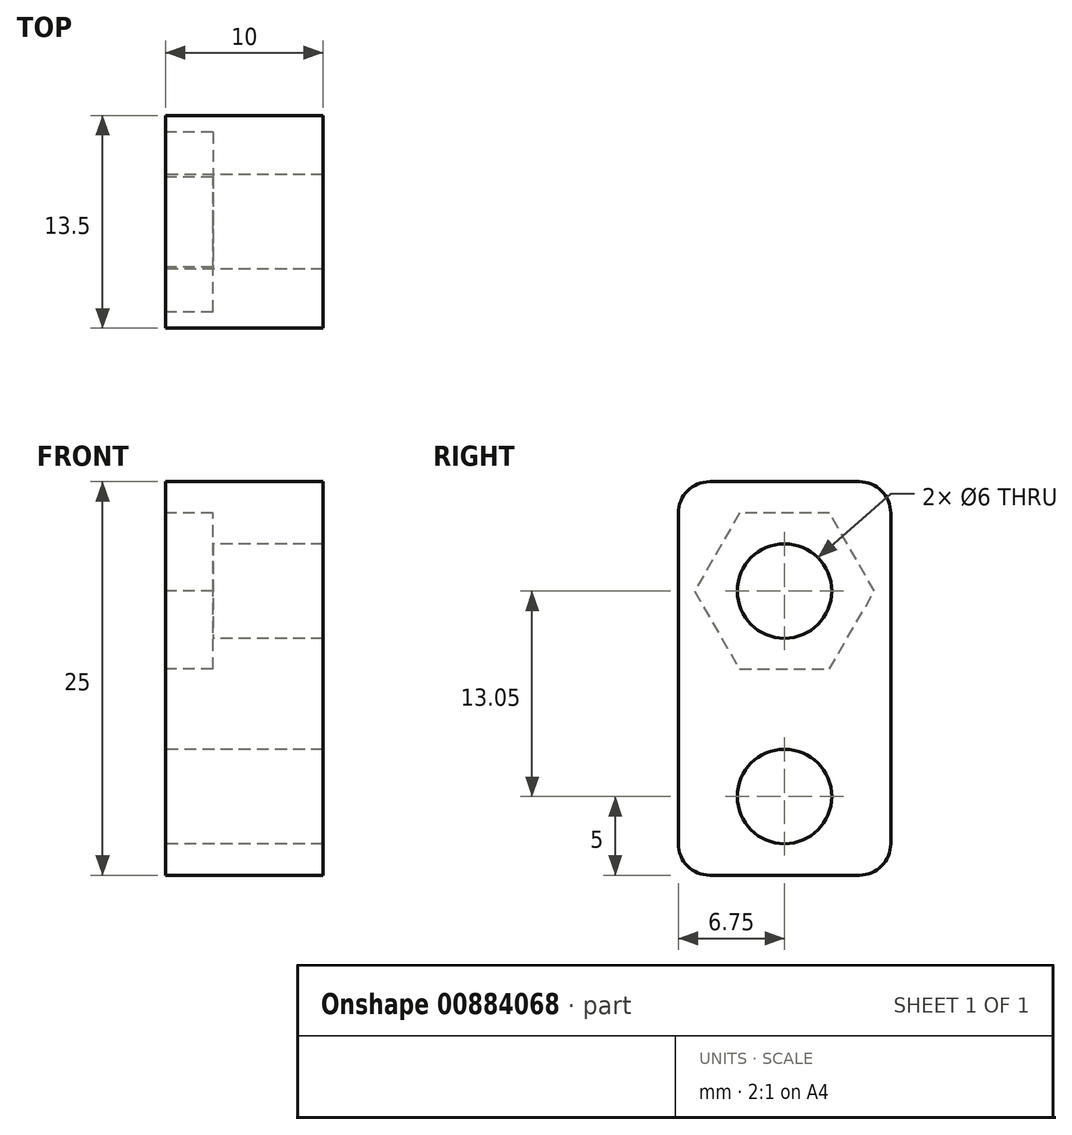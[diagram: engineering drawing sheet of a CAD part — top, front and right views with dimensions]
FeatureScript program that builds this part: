
annotation { "Feature Type Name" : "Feature", "Feature Type Description" : "" }
export const myFeature = defineFeature(function(context is Context, id is Id, definition is map)
    precondition{}
    {
        {
            var Q0;
            Q0=qCreatedBy(makeId("Top.planeOp"),FACE);
            var sketch = newSketch(context, id + "F0", { "sketchPlane" : qUnion([Q0])});
            skLineSegment(sketch, "E0.bottom", {"start": v(5, 6.75) * mm, "end": v(-5, 6.75) * mm});
            skLineSegment(sketch, "E0.top", {"start": v(5, -6.75) * mm, "end": v(-5, -6.75) * mm});
            skLineSegment(sketch, "E0.left", {"start": v(5, 6.75) * mm, "end": v(5, -6.75) * mm});
            skLineSegment(sketch, "E0.right", {"start": v(-5, 6.75) * mm, "end": v(-5, -6.75) * mm});
            skPoint(sketch, "E0.middle", {"position": v(0, 0) * mm});
            skSolve(sketch);
        }
        {
            var Q0;
            Q0 = qSketchRegion(id + "F0", true);
            extrude(context, id + "F1", {"entities" : qUnion([Q0]), "depth" : 25 * mm, "offsetDistance" : 25 * mm});
        }
        {
            var Q0;
            Q0=makeQuery(id+"F1.opExtrude","SWEPT_FACE",FACE,{"disambiguationData":[OSD([sQuery(id+"F0.wireOp",EDGE,"E0.right")])]});
            var sketch = newSketch(context, id + "F2", { "sketchPlane" : qUnion([Q0])});
            skCircle(sketch, "E1.cCircle", {"center": v(0, 18.05) * mm, "radius": 4.95 * mm, "construction": true});
            skLineSegment(sketch, "E1.0", {"start": v(-2.86, 23) * mm, "end": v(2.86, 23) * mm});
            skLineSegment(sketch, "E1.1", {"start": v(2.86, 23) * mm, "end": v(5.72, 18.05) * mm});
            skLineSegment(sketch, "E1.2", {"start": v(5.72, 18.05) * mm, "end": v(2.86, 13.1) * mm});
            skLineSegment(sketch, "E1.3", {"start": v(2.86, 13.1) * mm, "end": v(-2.86, 13.1) * mm});
            skLineSegment(sketch, "E1.4", {"start": v(-2.86, 13.1) * mm, "end": v(-5.72, 18.05) * mm});
            skLineSegment(sketch, "E1.5", {"start": v(-5.72, 18.05) * mm, "end": v(-2.86, 23) * mm});
            skPoint(sketch, "E1.0.midPoint", {"position": v(0, 23) * mm});
            skCircle(sketch, "E2", {"center": v(0, 5) * mm, "radius": 3 * mm});
            skCircle(sketch, "E3", {"center": v(0, 18.05) * mm, "radius": 3 * mm});
            skSolve(sketch);
        }
        {
            var Q0;
            Q0=makeQuery(id+"F2.imprint","IMPRINT",FACE,{"disambiguationData":[TD([[makeQuery(id+"F2.imprint","IMPRINT",EDGE,{"derivedFrom":sQuery(id+"F2.wireOp",EDGE,"E1.0")}),-1.0]])]});
            extrude(context, id + "F3", {"entities" : qUnion([Q0]), "operationType" : NewBodyOperationType.REMOVE, "oppositeDirection" : true, "depth" : 3 * mm, "offsetDistance" : 25 * mm});
        }
        {
            var Q0;
            Q0=makeQuery(id+"F2.imprint","IMPRINT",FACE,{"disambiguationData":[TD([[makeQuery(id+"F2.imprint","IMPRINT",EDGE,{"derivedFrom":sQuery(id+"F2.wireOp",EDGE,"E2")}),1.0]])]});
            var Q1;
            Q1=makeQuery(id+"F2.imprint","IMPRINT",FACE,{"disambiguationData":[TD([[makeQuery(id+"F2.imprint","IMPRINT",EDGE,{"derivedFrom":sQuery(id+"F2.wireOp",EDGE,"E3")}),1.0]])]});
            extrude(context, id + "F4", {"entities" : qUnion([Q0, Q1]), "operationType" : NewBodyOperationType.REMOVE, "oppositeDirection" : true, "depth" : 25 * mm, "offsetDistance" : 25 * mm});
        }
        {
            var Q0;
            Q0=makeQuery(id+"F1.opExtrude","CAP_EDGE",EDGE,{"disambiguationData":[OSD([sQuery(id+"F0.wireOp",EDGE,"E0.top")])],"isStart":false});
            var Q1;
            Q1=makeQuery(id+"F1.opExtrude","CAP_EDGE",EDGE,{"disambiguationData":[OSD([sQuery(id+"F0.wireOp",EDGE,"E0.bottom")])],"isStart":false});
            var Q2;
            Q2=makeQuery(id+"F1.opExtrude","CAP_EDGE",EDGE,{"disambiguationData":[OSD([sQuery(id+"F0.wireOp",EDGE,"E0.top")])],"isStart":true});
            var Q3;
            Q3=makeQuery(id+"F1.opExtrude","CAP_EDGE",EDGE,{"disambiguationData":[OSD([sQuery(id+"F0.wireOp",EDGE,"E0.bottom")])],"isStart":true});
            fillet(context, id + "F5", {"entities" : qUnion([Q0, Q1, Q2, Q3]), "radius" : 2 * mm, "tangentPropagation" : true, "allowEdgeOverflow" : false});
        }
    });
